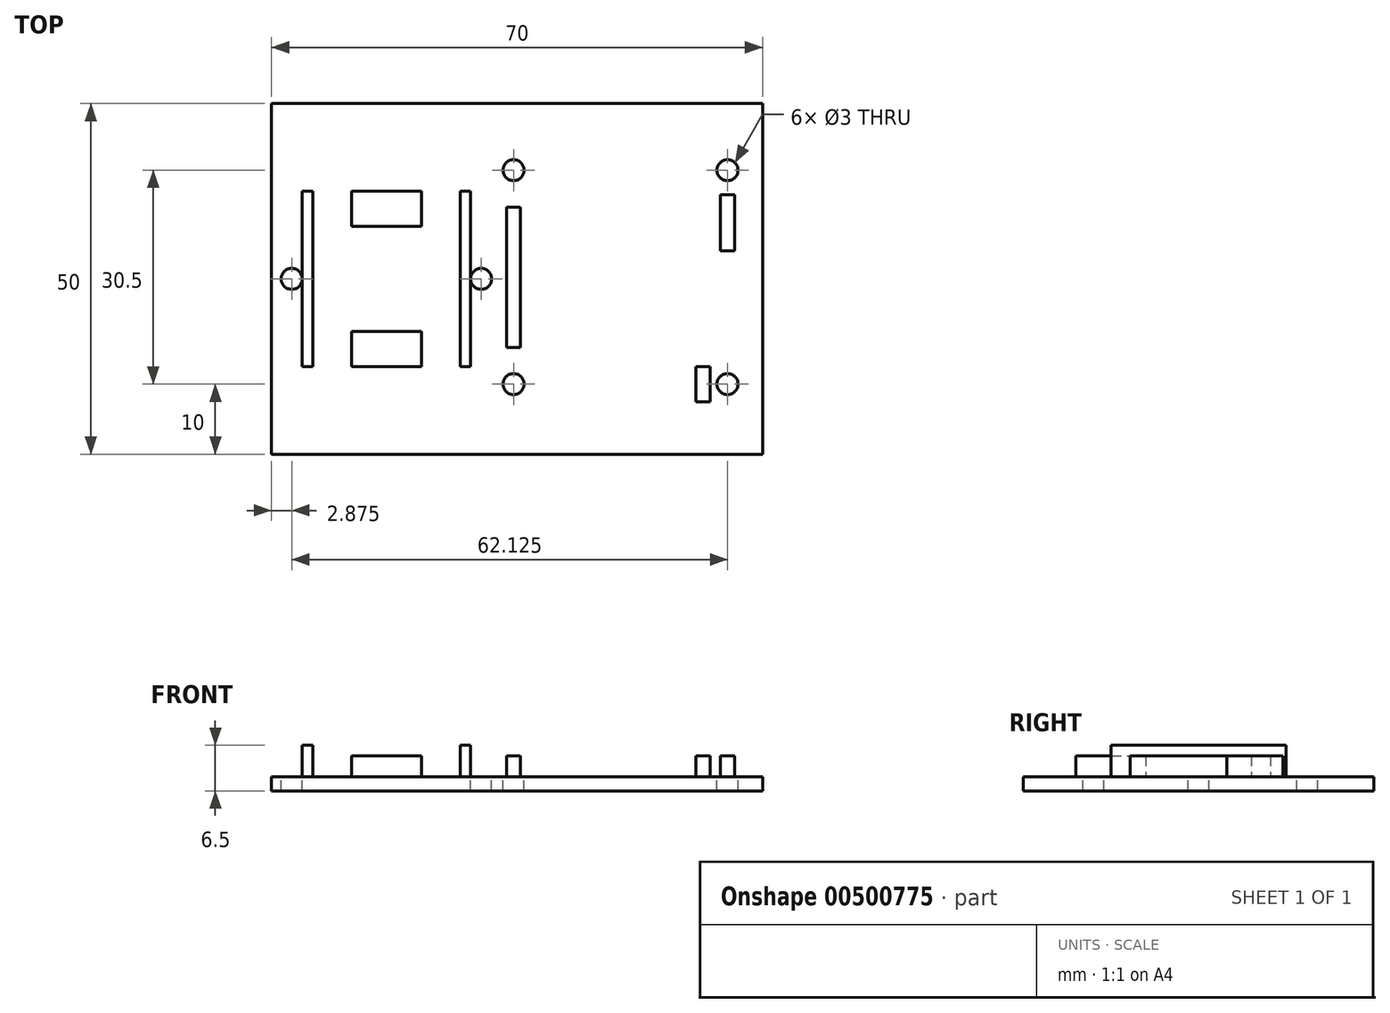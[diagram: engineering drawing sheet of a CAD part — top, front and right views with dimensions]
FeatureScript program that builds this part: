
annotation { "Feature Type Name" : "Feature", "Feature Type Description" : "" }
export const myFeature = defineFeature(function(context is Context, id is Id, definition is map)
    precondition{}
    {
        {
            var Q0;
            Q0=qCreatedBy(makeId("Top.planeOp"),FACE);
            var sketch = newSketch(context, id + "F0", { "sketchPlane" : qUnion([Q0])});
            skLineSegment(sketch, "E0.bottom", {"start": v(35, 25) * mm, "end": v(-35, 25) * mm});
            skLineSegment(sketch, "E0.top", {"start": v(35, -25) * mm, "end": v(-35, -25) * mm});
            skLineSegment(sketch, "E0.left", {"start": v(35, 25) * mm, "end": v(35, -25) * mm});
            skLineSegment(sketch, "E0.right", {"start": v(-35, 25) * mm, "end": v(-35, -25) * mm});
            skPoint(sketch, "E0.middle", {"position": v(0, 0) * mm});
            skSolve(sketch);
        }
        {
            var Q0;
            Q0=makeQuery(id+"F0.imprint","IMPRINT",FACE,{"disambiguationData":[TD([[makeQuery(id+"F0.imprint","IMPRINT",EDGE,{"derivedFrom":sQuery(id+"F0.wireOp",EDGE,"E0.bottom")}),1.0]])]});
            extrude(context, id + "F1", {"entities" : qUnion([Q0]), "depth" : 2 * mm});
        }
        {
            var Q0;
            Q0=makeQuery(id+"F1.opExtrude","CAP_FACE",FACE,{"disambiguationData":[OSD([sQuery(id+"F0.wireOp",EDGE,"E0.bottom"),sQuery(id+"F0.wireOp",EDGE,"E0.top"),sQuery(id+"F0.wireOp",EDGE,"E0.left"),sQuery(id+"F0.wireOp",EDGE,"E0.right")])],"isStart":false});
            var sketch = newSketch(context, id + "F2", { "sketchPlane" : qUnion([Q0])});
            skLineSegment(sketch, "E1.bottom", {"start": v(30, 15.5) * mm, "end": v(-0.5, 15.5) * mm, "construction": true});
            skLineSegment(sketch, "E1.top", {"start": v(30, -15) * mm, "end": v(-0.5, -15) * mm, "construction": true});
            skLineSegment(sketch, "E1.left", {"start": v(30, 15.5) * mm, "end": v(30, -15) * mm, "construction": true});
            skLineSegment(sketch, "E1.right", {"start": v(-0.5, 15.5) * mm, "end": v(-0.5, -15) * mm, "construction": true});
            skPoint(sketch, "E1.middle", {"position": v(14.75, 0.25) * mm});
            skLineSegment(sketch, "E2.bottom", {"start": v(0.5, 10.25) * mm, "end": v(-1.5, 10.25) * mm});
            skLineSegment(sketch, "E2.top", {"start": v(0.5, -9.75) * mm, "end": v(-1.5, -9.75) * mm});
            skLineSegment(sketch, "E2.left", {"start": v(0.5, 10.25) * mm, "end": v(0.5, -9.75) * mm});
            skLineSegment(sketch, "E2.right", {"start": v(-1.5, 10.25) * mm, "end": v(-1.5, -9.75) * mm});
            skPoint(sketch, "E2.middle", {"position": v(-0.5, 0.25) * mm});
            skLineSegment(sketch, "E3.bottom", {"start": v(31, 4) * mm, "end": v(29, 4) * mm});
            skLineSegment(sketch, "E3.top", {"start": v(31, 12) * mm, "end": v(29, 12) * mm});
            skLineSegment(sketch, "E3.left", {"start": v(31, 4) * mm, "end": v(31, 12) * mm});
            skLineSegment(sketch, "E3.right", {"start": v(29, 4) * mm, "end": v(29, 12) * mm});
            skPoint(sketch, "E3.middle", {"position": v(30, 8) * mm});
            skLineSegment(sketch, "E4.bottom", {"start": v(27.5, -17.5) * mm, "end": v(25.5, -17.5) * mm});
            skLineSegment(sketch, "E4.top", {"start": v(27.5, -12.5) * mm, "end": v(25.5, -12.5) * mm});
            skLineSegment(sketch, "E4.left", {"start": v(27.5, -17.5) * mm, "end": v(27.5, -12.5) * mm});
            skLineSegment(sketch, "E4.right", {"start": v(25.5, -17.5) * mm, "end": v(25.5, -12.5) * mm});
            skPoint(sketch, "E4.middle", {"position": v(26.5, -15) * mm});
            skSolve(sketch);
        }
        {
            var Q0;
            Q0=makeQuery(id+"F2.imprint","IMPRINT",FACE,{"disambiguationData":[TD([[makeQuery(id+"F2.imprint","IMPRINT",EDGE,{"derivedFrom":makeQuery(id+"F1.opExtrude","CAP_EDGE",EDGE,{"disambiguationData":[OSD([sQuery(id+"F0.wireOp",EDGE,"E0.bottom")])],"isStart":false})}),1.0]])]});
            var sketch = newSketch(context, id + "F3", { "sketchPlane" : qUnion([Q0])});
            skLineSegment(sketch, "E5.bottom", {"start": v(-8.25, -21.68) * mm, "end": v(-29, -21.68) * mm, "construction": true});
            skLineSegment(sketch, "E5.top", {"start": v(-8.25, 21.67) * mm, "end": v(-29, 21.68) * mm, "construction": true});
            skLineSegment(sketch, "E5.left", {"start": v(-8.25, -21.68) * mm, "end": v(-8.25, 21.68) * mm, "construction": true});
            skLineSegment(sketch, "E5.right", {"start": v(-29, -21.68) * mm, "end": v(-29, 21.68) * mm, "construction": true});
            skPoint(sketch, "E5.middle", {"position": v(-18.63, 0) * mm});
            skPoint(sketch, "E6", {"position": v(-29, 0) * mm});
            skPoint(sketch, "E7", {"position": v(-8.25, 0) * mm});
            skLineSegment(sketch, "E8", {"start": v(-18.63, 0) * mm, "end": v(-18.63, 10) * mm, "construction": true});
            skLineSegment(sketch, "E9", {"start": v(-18.63, 0) * mm, "end": v(-18.63, -10) * mm, "construction": true});
            skLineSegment(sketch, "E10.bottom", {"start": v(-13.63, 12.5) * mm, "end": v(-23.63, 12.5) * mm});
            skLineSegment(sketch, "E10.top", {"start": v(-13.63, 7.5) * mm, "end": v(-23.63, 7.5) * mm});
            skLineSegment(sketch, "E10.left", {"start": v(-13.63, 12.5) * mm, "end": v(-13.63, 7.5) * mm});
            skLineSegment(sketch, "E10.right", {"start": v(-23.63, 12.5) * mm, "end": v(-23.63, 7.5) * mm});
            skPoint(sketch, "E10.middle", {"position": v(-18.63, 10) * mm});
            skLineSegment(sketch, "E11.MirrorCS", {"start": v(-13.63, -7.5) * mm, "end": v(-23.63, -7.5) * mm});
            skLineSegment(sketch, "E12.MirrorCS", {"start": v(-23.63, -12.5) * mm, "end": v(-23.63, -7.5) * mm});
            skLineSegment(sketch, "E13.MirrorCS", {"start": v(-13.63, -12.5) * mm, "end": v(-23.63, -12.5) * mm});
            skLineSegment(sketch, "E14.MirrorCS", {"start": v(-13.63, -12.5) * mm, "end": v(-13.63, -7.5) * mm});
            skLineSegment(sketch, "E15.bottom", {"start": v(-6.63, 12.5) * mm, "end": v(-8.13, 12.5) * mm});
            skLineSegment(sketch, "E15.top", {"start": v(-6.63, -12.5) * mm, "end": v(-8.13, -12.5) * mm});
            skLineSegment(sketch, "E15.left", {"start": v(-6.63, 12.5) * mm, "end": v(-6.63, -12.5) * mm});
            skLineSegment(sketch, "E15.right", {"start": v(-8.13, 12.5) * mm, "end": v(-8.13, -12.5) * mm});
            skPoint(sketch, "E15.middle", {"position": v(-7.38, 0) * mm});
            skLineSegment(sketch, "E16.MirrorCS", {"start": v(-29.13, 12.5) * mm, "end": v(-29.13, -12.5) * mm});
            skLineSegment(sketch, "E17.MirrorCS", {"start": v(-30.63, 12.5) * mm, "end": v(-29.13, 12.5) * mm});
            skLineSegment(sketch, "E18.MirrorCS", {"start": v(-30.62, 12.5) * mm, "end": v(-30.62, -12.5) * mm});
            skLineSegment(sketch, "E19.MirrorCS", {"start": v(-30.63, -12.5) * mm, "end": v(-29.12, -12.5) * mm});
            skLineSegment(sketch, "E20", {"start": v(-18.63, 0) * mm, "end": v(-5.13, 0) * mm});
            skPoint(sketch, "E20.endSnap0", {"position": v(-6.63, 0) * mm});
            skLineSegment(sketch, "E21", {"start": v(-18.63, 0) * mm, "end": v(-32.12, 0) * mm});
            skSolve(sketch);
        }
        {
            var Q0;
            Q0=makeQuery(id+"F3.imprint","IMPRINT",FACE,{"disambiguationData":[TD([[makeQuery(id+"F3.imprint","IMPRINT",EDGE,{"derivedFrom":sQuery(id+"F3.wireOp",EDGE,"E16.MirrorCS")}),-1.0]])]});
            var Q1;
            {var subQ0=sQuery(id+"F3.wireOp",EDGE,"E15.bottom");Q1=makeQuery(id+"F3.imprint","IMPRINT",FACE,{"disambiguationData":[TD([[makeQuery(id+"F3.imprint","IMPRINT",EDGE,{"derivedFrom":subQ0}),1.0]])]});}
            var Q2;
            {var subQ0=sQuery(id+"F3.wireOp",EDGE,"E15.top");Q2=makeQuery(id+"F3.imprint","IMPRINT",FACE,{"disambiguationData":[TD([[makeQuery(id+"F3.imprint","IMPRINT",EDGE,{"derivedFrom":subQ0}),-1.0]])]});}
            extrude(context, id + "F4", {"entities" : qUnion([Q0, Q1, Q2]), "operationType" : NewBodyOperationType.ADD, "depth" : 4.5 * mm});
        }
        {
            var Q0;
            Q0=sQuery(id+"F2.wireOp",VERTEX,"E1.right.start");
            var Q1;
            Q1=sQuery(id+"F2.wireOp",VERTEX,"E1.left.start");
            var Q2;
            Q2=sQuery(id+"F2.wireOp",VERTEX,"E1.left.end");
            var Q3;
            Q3=sQuery(id+"F2.wireOp",VERTEX,"E1.top.end");
            var Q4;
            Q4=sQuery(id+"F3.wireOp",VERTEX,"E20.end");
            var Q5;
            Q5=sQuery(id+"F3.wireOp",VERTEX,"E21.end");
            var Q6;
            Q6=makeQuery(id+"F1.opExtrude","SWEPT_BODY",BODY,{"disambiguationData":[OSD([sQuery(id+"F0.wireOp",EDGE,"E0.bottom"),sQuery(id+"F0.wireOp",EDGE,"E0.top"),sQuery(id+"F0.wireOp",EDGE,"E0.left"),sQuery(id+"F0.wireOp",EDGE,"E0.right")])]});
            hole(context, id + "F5", {"style" : HoleStyle.SIMPLE, "endStyle" : HoleEndStyle.BLIND, "holeDiameter" : 3 * mm, "holeDepth" : 10 * mm, "isTappedThrough" : true, "tappedDepth" : 12 * mm, "tapClearance" : 3, "locations" : qUnion([Q0, Q1, Q2, Q3, Q4, Q5]), "scope" : qUnion([Q6])});
        }
        {
            var Q0;
            Q0=makeQuery(id+"F3.imprint","IMPRINT",FACE,{"disambiguationData":[TD([[makeQuery(id+"F3.imprint","IMPRINT",EDGE,{"derivedFrom":sQuery(id+"F3.wireOp",EDGE,"E10.bottom")}),1.0]])]});
            var Q1;
            Q1=makeQuery(id+"F3.imprint","IMPRINT",FACE,{"disambiguationData":[TD([[makeQuery(id+"F3.imprint","IMPRINT",EDGE,{"derivedFrom":sQuery(id+"F3.wireOp",EDGE,"E11.MirrorCS")}),1.0]])]});
            var Q2;
            Q2=makeQuery(id+"F3.imprint","IMPRINT",FACE,{"disambiguationData":[TD([[makeQuery(id+"F3.imprint","IMPRINT",EDGE,{"derivedFrom":makeQuery(id+"F2.imprint","IMPRINT",EDGE,{"derivedFrom":sQuery(id+"F2.wireOp",EDGE,"E4.bottom")})}),-1.0]])]});
            var Q3;
            Q3=makeQuery(id+"F3.imprint","IMPRINT",FACE,{"disambiguationData":[TD([[makeQuery(id+"F3.imprint","IMPRINT",EDGE,{"derivedFrom":makeQuery(id+"F2.imprint","IMPRINT",EDGE,{"derivedFrom":sQuery(id+"F2.wireOp",EDGE,"E3.bottom")})}),-1.0]])]});
            var Q4;
            Q4=makeQuery(id+"F3.imprint","IMPRINT",FACE,{"disambiguationData":[TD([[makeQuery(id+"F3.imprint","IMPRINT",EDGE,{"derivedFrom":makeQuery(id+"F2.imprint","IMPRINT",EDGE,{"derivedFrom":sQuery(id+"F2.wireOp",EDGE,"E2.bottom")})}),1.0]])]});
            var Q5;
            Q5 = qConstructionFilter(qBodyType(qCreatedBy(id + "F3" ,EDGE), BodyType.WIRE), ConstructionObject.NO);
            extrude(context, id + "F6", {"entities" : qUnion([Q0, Q1, Q2, Q3, Q4]), "operationType" : NewBodyOperationType.ADD, "surfaceEntities" : qUnion([Q5]), "depth" : 3 * mm});
        }
    });
